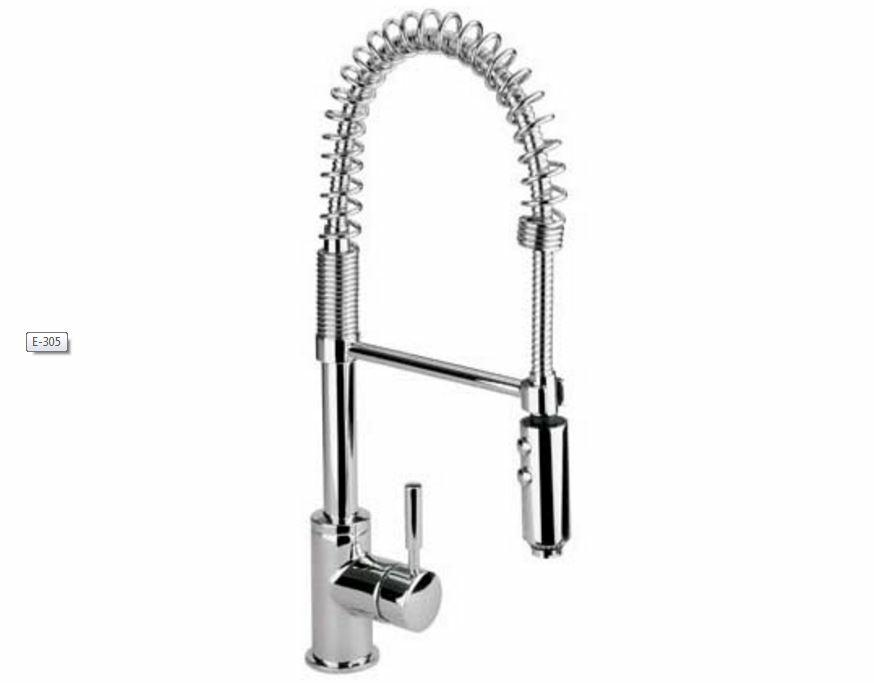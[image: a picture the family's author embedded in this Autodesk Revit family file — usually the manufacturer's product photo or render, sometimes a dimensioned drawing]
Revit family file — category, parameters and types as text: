
# Revit family: Monomando de Cocina E-307
name_source: partatom
category: Mobiliario
revit_build: Autodesk Revit 2016 (Build: 20150220_1215(x64)
units: mm (PartAtom-declared; Revit-internal decimal feet)

## family parameters
Compartido = Sí
Corte con vacíos al cargar = No
Número OmniClass = 23.45.55.14
Punto de cálculo de habitación = Sí
Se basa en plano de trabajo = No
Siempre vertical = Sí
Título OmniClass = Single Faucets

## types (1)
- E-307
    Brass Chromed = Brass
    Comentarios de tipo = Single Control Kitchen Faucet
    Data Sheet = http://www.helvex.com.mx
    Descripción = Single Control With Flexible Faucet
    Elevación por Defecto = 1"
    Fabricante = HELVEX
    Features = Single Control Ceramic Cartridge; Giratory Faucet; Device To Change a Fixed Jet Shower; Flexible Hose And Head; Includes Wrench to Install
    Imagen de tipo = E-305.JPG
    Inlet Threads = ½" - 14 NPSM
    Instructive = http://www.helvex.com.mx
    Max. Working Pressure = 85.3 psi
    Min. Working Pressure = 14.2 psi
    Modelo = E-305
    Total Height = 14"
    Total Length = 12"
    Total Width = 5"
    URL = http://www.helvex.com.mx

## geometry (parser evidence)
native form markers: Sweep x3
no freeform markers — native parametric forms only
